# Revit family: URBANE II CF INVISI WF 4S SUITE + OLIDA SC SEAT
name_source: partatom
category: Specialty Equipment
units: mm (PartAtom-declared; Revit-internal decimal feet)

## family parameters
Cut with Voids When Loaded = No
Host = Face
OmniClass Number = 23.45.05.21.11.11
OmniClass Title = Water Operated Water Closets
Part Type = Normal
Room Calculation Point = No
Round Connector Dimension = Use Radius
Shared = No

## types (1)
- URBANE II CF INVISI WF 4S SUITE + OLIDA SC SEAT
    Assembly Code = D2010110
    Default Elevation = 0 mm  [stored 0 ft]
    Description = URBANE II CF INVISI WF 4S SUITE + OLIDA SC SEAT
    Manufacturer = GWA Bathrooms & Kitchens
    Material_Base = GWA-Porcelain-White
    Material_Buttons = GWA_Metal-Stainless
    Material_Fixing = GWA_Metal-Stainless
    Material_Seat = GWA-Acrylic-White
    Model = 746280W
    URL = https://www.caroma.com.au

note: [stored X ft] marks values corroborated as IEEE doubles in the binary element streams (Revit-internal decimal feet)

## geometry (parser evidence)
native form markers: Sweep x2
no freeform markers — native parametric forms only
